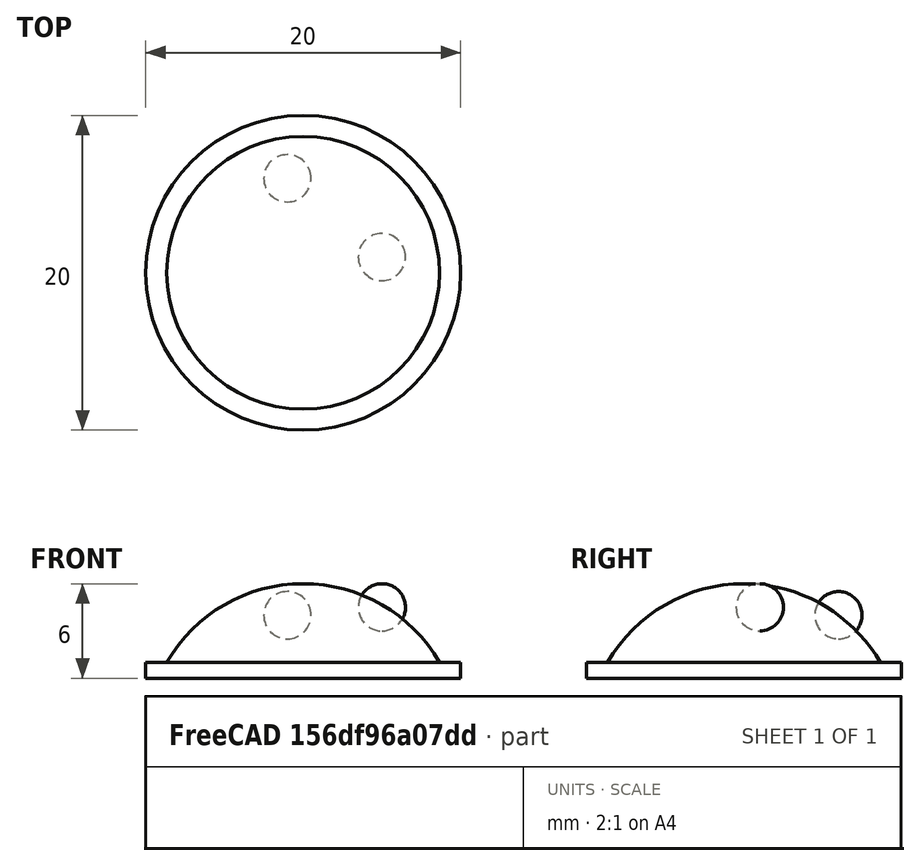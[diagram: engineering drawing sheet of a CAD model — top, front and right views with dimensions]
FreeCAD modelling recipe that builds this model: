
FCSTD DOCUMENT  (FreeCAD 1.0R39319 (Git))
Label: ojt1_t13r01_robot
License: All rights reserved
LicenseURL: https://en.wikipedia.org/wiki/All_rights_reserved
objects: Part::Sphere×3, Part::MultiFuse×2, Part::Cylinder×1
note: 6 computed .brp shape members not serialized (recipe doc carries the construction recipe); baked Part::Feature solids carry a one-line shape summary decoded from their .brp

FEATURE [Part::Sphere] Sphere
  Angle1 = 25
  Angle2 = 90
  Angle3 = 360
  AttacherType = Attacher::AttachEngine3D
  Placement = pos=(0,0,-4) rot=(0,0,1;0rad)
  Radius = 10
FEATURE [Part::Cylinder] Cylinder
  Angle = 360
  AttacherType = Attacher::AttachEngine3D
  FirstAngle = 0
  Height = 1
  Radius = 10
  SecondAngle = 0
FEATURE [Part::MultiFuse] Fusion
  Refine = true
  Shapes = -> [Sphere,Cylinder]
FEATURE [Part::Sphere] Sphere001
  Angle1 = -90
  Angle2 = 90
  Angle3 = 360
  AttacherType = Attacher::AttachEngine3D
  Placement = pos=(5,1,4.5) rot=(0,0,1;0rad)
  Radius = 1.5
FEATURE [Part::Sphere] Sphere002
  Angle1 = -90
  Angle2 = 90
  Angle3 = 360
  AttacherType = Attacher::AttachEngine3D
  Placement = pos=(-1,6,4) rot=(0,0,1;0rad)
  Radius = 1.5
FEATURE [Part::MultiFuse] Fusion001
  Refine = true
  Shapes = -> [Sphere002,Sphere001]
